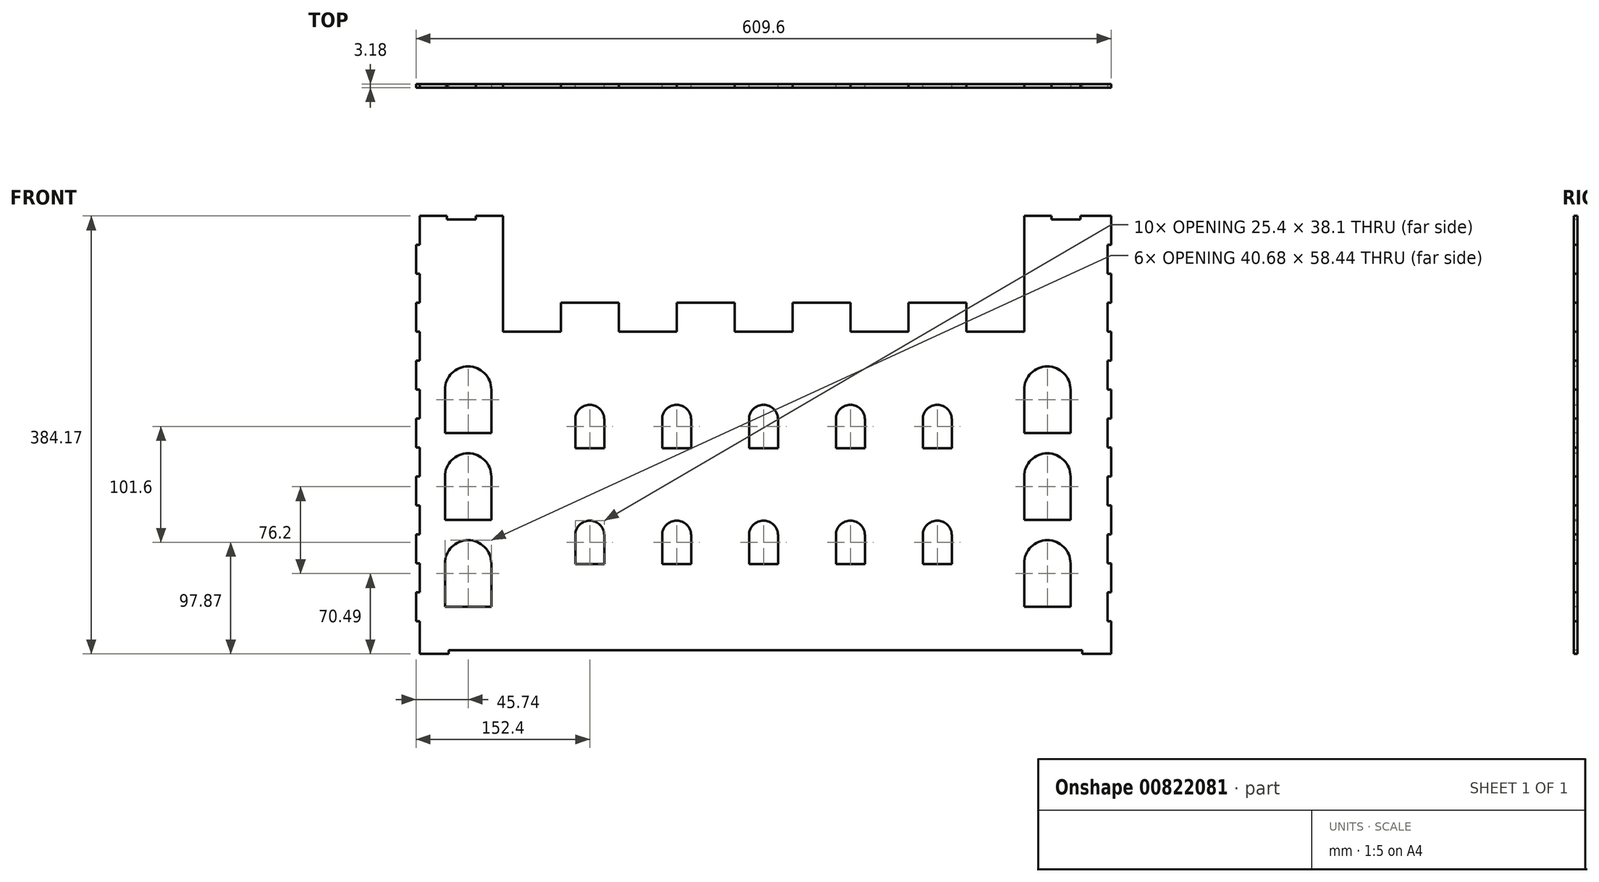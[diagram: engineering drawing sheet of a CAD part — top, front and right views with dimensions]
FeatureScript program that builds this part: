
annotation { "Feature Type Name" : "Feature", "Feature Type Description" : "" }
export const myFeature = defineFeature(function(context is Context, id is Id, definition is map)
    precondition{}
    {
        {
            var Q0;
            Q0=qCreatedBy(makeId("Front.planeOp"),FACE);
            var sketch = newSketch(context, id + "F0", { "sketchPlane" : qUnion([Q0])});
            skLineSegment(sketch, "E0.bottom", {"start": v(-304.8, 152.4) * mm, "end": v(-228.6, 152.4) * mm});
            skLineSegment(sketch, "E0.top", {"start": v(-304.8, -152.4) * mm, "end": v(304.8, -152.4) * mm});
            skLineSegment(sketch, "E0.left", {"start": v(-304.8, 152.4) * mm, "end": v(-304.8, -152.4) * mm});
            skLineSegment(sketch, "E0.right", {"start": v(304.8, 152.4) * mm, "end": v(304.8, -152.4) * mm});
            skPoint(sketch, "E0.middle", {"position": v(0, 0) * mm});
            skLineSegment(sketch, "E1", {"start": v(-304.8, 152.4) * mm, "end": v(-304.8, 228.6) * mm});
            skLineSegment(sketch, "E2", {"start": v(-304.8, 228.6) * mm, "end": v(-228.6, 228.6) * mm});
            skLineSegment(sketch, "E3", {"start": v(-228.6, 228.6) * mm, "end": v(-228.6, 152.4) * mm});
            skLineSegment(sketch, "E4", {"start": v(304.8, 152.4) * mm, "end": v(304.8, 228.6) * mm});
            skLineSegment(sketch, "E5", {"start": v(304.8, 228.6) * mm, "end": v(228.6, 228.6) * mm});
            skLineSegment(sketch, "E6", {"start": v(228.6, 228.6) * mm, "end": v(228.6, 152.4) * mm});
            skLineSegment(sketch, "E7", {"start": v(-228.6, 152.4) * mm, "end": v(-228.6, 127) * mm});
            skLineSegment(sketch, "E8", {"start": v(-228.6, 127) * mm, "end": v(-177.8, 127) * mm});
            skLineSegment(sketch, "E9", {"start": v(-177.8, 127) * mm, "end": v(-177.8, 152.4) * mm});
            skLineSegment(sketch, "E10.1.0.0", {"start": v(-76.2, 127) * mm, "end": v(-76.2, 152.4) * mm});
            skLineSegment(sketch, "E10.1.0.1", {"start": v(-127, 152.4) * mm, "end": v(-127, 127) * mm});
            skLineSegment(sketch, "E10.1.0.2", {"start": v(-127, 127) * mm, "end": v(-76.2, 127) * mm});
            skLineSegment(sketch, "E10.2.0.0", {"start": v(25.4, 127) * mm, "end": v(25.4, 152.4) * mm});
            skLineSegment(sketch, "E10.2.0.1", {"start": v(-25.4, 152.4) * mm, "end": v(-25.4, 127) * mm});
            skLineSegment(sketch, "E10.2.0.2", {"start": v(-25.4, 127) * mm, "end": v(25.4, 127) * mm});
            skLineSegment(sketch, "E10.3.0.0", {"start": v(127, 127) * mm, "end": v(127, 152.4) * mm});
            skLineSegment(sketch, "E10.3.0.1", {"start": v(76.2, 152.4) * mm, "end": v(76.2, 127) * mm});
            skLineSegment(sketch, "E10.3.0.2", {"start": v(76.2, 127) * mm, "end": v(127, 127) * mm});
            skLineSegment(sketch, "E10.4.0.0", {"start": v(228.6, 127) * mm, "end": v(228.6, 152.4) * mm});
            skLineSegment(sketch, "E10.4.0.1", {"start": v(177.8, 152.4) * mm, "end": v(177.8, 127) * mm});
            skLineSegment(sketch, "E10.4.0.2", {"start": v(177.8, 127) * mm, "end": v(228.6, 127) * mm});
            skLineSegment(sketch, "E10.direction1", {"start": v(-177.8, 127) * mm, "end": v(-76.2, 127) * mm, "construction": true});
            skLineSegment(sketch, "E11.trimOffspring", {"start": v(-177.8, 152.4) * mm, "end": v(-127, 152.4) * mm});
            skLineSegment(sketch, "E12.trimOffspring", {"start": v(-76.2, 152.4) * mm, "end": v(-25.4, 152.4) * mm});
            skLineSegment(sketch, "E13.trimOffspring", {"start": v(25.4, 152.4) * mm, "end": v(76.2, 152.4) * mm});
            skLineSegment(sketch, "E14.trimOffspring", {"start": v(127, 152.4) * mm, "end": v(177.8, 152.4) * mm});
            skLineSegment(sketch, "E15.trimOffspring", {"start": v(228.6, 152.4) * mm, "end": v(304.8, 152.4) * mm});
            skSolve(sketch);
        }
        {
            var Q0;
            Q0 = qSketchRegion(id + "F0", true);
            extrude(context, id + "F1", {"entities" : qUnion([Q0]), "depth" : 3.17 * mm, "offsetDistance" : 25.4 * mm});
        }
        {
            var Q0;
            Q0=makeQuery(id+"F1.opExtrude","CAP_FACE",FACE,{"disambiguationData":[OSD([sQuery(id+"F0.wireOp",EDGE,"E0.top"),sQuery(id+"F0.wireOp",EDGE,"E0.left"),sQuery(id+"F0.wireOp",EDGE,"E0.right"),sQuery(id+"F0.wireOp",EDGE,"E1"),sQuery(id+"F0.wireOp",EDGE,"E2"),sQuery(id+"F0.wireOp",EDGE,"E3"),sQuery(id+"F0.wireOp",EDGE,"E4"),sQuery(id+"F0.wireOp",EDGE,"E5"),sQuery(id+"F0.wireOp",EDGE,"E6"),sQuery(id+"F0.wireOp",EDGE,"E7"),sQuery(id+"F0.wireOp",EDGE,"E8"),sQuery(id+"F0.wireOp",EDGE,"E9"),sQuery(id+"F0.wireOp",EDGE,"E10.1.0.0"),sQuery(id+"F0.wireOp",EDGE,"E10.1.0.1"),sQuery(id+"F0.wireOp",EDGE,"E10.1.0.2"),sQuery(id+"F0.wireOp",EDGE,"E10.2.0.0"),sQuery(id+"F0.wireOp",EDGE,"E10.2.0.1"),sQuery(id+"F0.wireOp",EDGE,"E10.2.0.2"),sQuery(id+"F0.wireOp",EDGE,"E10.3.0.0"),sQuery(id+"F0.wireOp",EDGE,"E10.3.0.1"),sQuery(id+"F0.wireOp",EDGE,"E10.3.0.2"),sQuery(id+"F0.wireOp",EDGE,"E10.4.0.0"),sQuery(id+"F0.wireOp",EDGE,"E10.4.0.1"),sQuery(id+"F0.wireOp",EDGE,"E10.4.0.2"),sQuery(id+"F0.wireOp",EDGE,"E11.trimOffspring"),sQuery(id+"F0.wireOp",EDGE,"E12.trimOffspring"),sQuery(id+"F0.wireOp",EDGE,"E13.trimOffspring"),sQuery(id+"F0.wireOp",EDGE,"E14.trimOffspring")])],"isStart":false});
            var sketch = newSketch(context, id + "F2", { "sketchPlane" : qUnion([Q0])});
            skLineSegment(sketch, "E16.bottom", {"start": v(-304.8, 127) * mm, "end": v(-301.63, 127) * mm});
            skLineSegment(sketch, "E16.top", {"start": v(-304.8, 101.6) * mm, "end": v(-301.63, 101.6) * mm});
            skLineSegment(sketch, "E16.left", {"start": v(-304.8, 127) * mm, "end": v(-304.8, 101.6) * mm});
            skLineSegment(sketch, "E16.right", {"start": v(-301.63, 127) * mm, "end": v(-301.63, 101.6) * mm});
            skLineSegment(sketch, "E17.0.1.0", {"start": v(-304.8, 76.2) * mm, "end": v(-301.63, 76.2) * mm});
            skLineSegment(sketch, "E17.0.1.1", {"start": v(-301.63, 76.2) * mm, "end": v(-301.63, 50.8) * mm});
            skLineSegment(sketch, "E17.0.1.2", {"start": v(-304.8, 50.8) * mm, "end": v(-301.63, 50.8) * mm});
            skLineSegment(sketch, "E17.0.2.0", {"start": v(-304.8, 25.4) * mm, "end": v(-301.63, 25.4) * mm});
            skLineSegment(sketch, "E17.0.2.1", {"start": v(-301.63, 25.4) * mm, "end": v(-301.63, 0) * mm});
            skLineSegment(sketch, "E17.0.2.2", {"start": v(-304.8, 0) * mm, "end": v(-301.63, 0) * mm});
            skLineSegment(sketch, "E17.0.3.0", {"start": v(-304.8, -25.4) * mm, "end": v(-301.63, -25.4) * mm});
            skLineSegment(sketch, "E17.0.3.1", {"start": v(-301.63, -25.4) * mm, "end": v(-301.63, -50.8) * mm});
            skLineSegment(sketch, "E17.0.3.2", {"start": v(-304.8, -50.8) * mm, "end": v(-301.63, -50.8) * mm});
            skLineSegment(sketch, "E17.0.4.0", {"start": v(-304.8, -76.2) * mm, "end": v(-301.63, -76.2) * mm});
            skLineSegment(sketch, "E17.0.4.1", {"start": v(-301.63, -76.2) * mm, "end": v(-301.63, -101.6) * mm});
            skLineSegment(sketch, "E17.0.4.2", {"start": v(-304.8, -101.6) * mm, "end": v(-301.63, -101.6) * mm});
            skLineSegment(sketch, "E17.0.5.0", {"start": v(-304.8, -127) * mm, "end": v(-301.63, -127) * mm});
            skLineSegment(sketch, "E17.0.5.1", {"start": v(-301.63, -127) * mm, "end": v(-301.63, -152.4) * mm});
            skLineSegment(sketch, "E17.0.5.2", {"start": v(-304.8, -152.4) * mm, "end": v(-301.63, -152.4) * mm});
            skLineSegment(sketch, "E17.direction1", {"start": v(-304.8, 127) * mm, "end": v(-279.4, 127) * mm, "construction": true});
            skLineSegment(sketch, "E17.direction2", {"start": v(-304.8, 127) * mm, "end": v(-304.8, 76.2) * mm, "construction": true});
            skLineSegment(sketch, "E18.0.1.0", {"start": v(-301.63, 177.8) * mm, "end": v(-301.63, 152.4) * mm});
            skLineSegment(sketch, "E18.0.1.1", {"start": v(-304.8, 152.4) * mm, "end": v(-301.63, 152.4) * mm});
            skLineSegment(sketch, "E18.0.2.0", {"start": v(-301.63, 228.6) * mm, "end": v(-301.63, 203.2) * mm});
            skLineSegment(sketch, "E18.0.2.1", {"start": v(-304.8, 203.2) * mm, "end": v(-301.63, 203.2) * mm});
            skLineSegment(sketch, "E18.direction1", {"start": v(-301.63, 101.6) * mm, "end": v(-276.23, 101.6) * mm, "construction": true});
            skLineSegment(sketch, "E18.direction2", {"start": v(-301.63, 101.6) * mm, "end": v(-301.63, 152.4) * mm, "construction": true});
            skLineSegment(sketch, "E19", {"start": v(-301.63, 177.8) * mm, "end": v(-304.8, 177.8) * mm});
            skLineSegment(sketch, "E20.bottom", {"start": v(304.8, 203.2) * mm, "end": v(301.63, 203.2) * mm});
            skLineSegment(sketch, "E20.top", {"start": v(304.8, 177.8) * mm, "end": v(301.63, 177.8) * mm});
            skLineSegment(sketch, "E20.left", {"start": v(304.8, 203.2) * mm, "end": v(304.8, 177.8) * mm});
            skLineSegment(sketch, "E20.right", {"start": v(301.63, 203.2) * mm, "end": v(301.63, 177.8) * mm});
            skLineSegment(sketch, "E21.0.1.0", {"start": v(304.8, 152.4) * mm, "end": v(301.63, 152.4) * mm});
            skLineSegment(sketch, "E21.0.1.1", {"start": v(301.63, 152.4) * mm, "end": v(301.63, 127) * mm});
            skLineSegment(sketch, "E21.0.1.2", {"start": v(304.8, 127) * mm, "end": v(301.63, 127) * mm});
            skLineSegment(sketch, "E21.0.2.0", {"start": v(304.8, 101.6) * mm, "end": v(301.63, 101.6) * mm});
            skLineSegment(sketch, "E21.0.2.1", {"start": v(301.63, 101.6) * mm, "end": v(301.63, 76.2) * mm});
            skLineSegment(sketch, "E21.0.2.2", {"start": v(304.8, 76.2) * mm, "end": v(301.63, 76.2) * mm});
            skLineSegment(sketch, "E21.0.3.0", {"start": v(304.8, 50.8) * mm, "end": v(301.63, 50.8) * mm});
            skLineSegment(sketch, "E21.0.3.1", {"start": v(301.63, 50.8) * mm, "end": v(301.63, 25.4) * mm});
            skLineSegment(sketch, "E21.0.3.2", {"start": v(304.8, 25.4) * mm, "end": v(301.63, 25.4) * mm});
            skLineSegment(sketch, "E21.0.4.0", {"start": v(304.8, 0) * mm, "end": v(301.63, 0) * mm});
            skLineSegment(sketch, "E21.0.4.1", {"start": v(301.63, 0) * mm, "end": v(301.63, -25.4) * mm});
            skLineSegment(sketch, "E21.0.4.2", {"start": v(304.8, -25.4) * mm, "end": v(301.63, -25.4) * mm});
            skLineSegment(sketch, "E21.0.5.0", {"start": v(304.8, -50.8) * mm, "end": v(301.63, -50.8) * mm});
            skLineSegment(sketch, "E21.0.5.1", {"start": v(301.63, -50.8) * mm, "end": v(301.63, -76.2) * mm});
            skLineSegment(sketch, "E21.0.5.2", {"start": v(304.8, -76.2) * mm, "end": v(301.63, -76.2) * mm});
            skLineSegment(sketch, "E21.0.6.0", {"start": v(304.8, -101.6) * mm, "end": v(301.63, -101.6) * mm});
            skLineSegment(sketch, "E21.0.6.1", {"start": v(301.63, -101.6) * mm, "end": v(301.63, -127) * mm});
            skLineSegment(sketch, "E21.0.6.2", {"start": v(304.8, -127) * mm, "end": v(301.63, -127) * mm});
            skLineSegment(sketch, "E21.direction1", {"start": v(301.63, 203.2) * mm, "end": v(327.03, 203.2) * mm, "construction": true});
            skLineSegment(sketch, "E21.direction2", {"start": v(301.63, 203.2) * mm, "end": v(301.63, 152.4) * mm, "construction": true});
            skSolve(sketch);
        }
        {
            var Q0;
            Q0 = qSketchRegion(id + "F2", true);
            var Q1;
            {var subQ0=sQuery(id+"F2.wireOp",EDGE,"E17.0.1.0");Q1=makeQuery(id+"F2.imprint","IMPRINT",FACE,{"disambiguationData":[TD([[makeQuery(id+"F2.imprint","IMPRINT",EDGE,{"derivedFrom":subQ0}),-1.0]])]});}
            var Q2;
            {var subQ0=sQuery(id+"F2.wireOp",EDGE,"E17.0.2.0");Q2=makeQuery(id+"F2.imprint","IMPRINT",FACE,{"disambiguationData":[TD([[makeQuery(id+"F2.imprint","IMPRINT",EDGE,{"derivedFrom":subQ0}),-1.0]])]});}
            var Q3;
            {var subQ0=sQuery(id+"F2.wireOp",EDGE,"E17.0.3.0");Q3=makeQuery(id+"F2.imprint","IMPRINT",FACE,{"disambiguationData":[TD([[makeQuery(id+"F2.imprint","IMPRINT",EDGE,{"derivedFrom":subQ0}),-1.0]])]});}
            var Q4;
            {var subQ0=sQuery(id+"F2.wireOp",EDGE,"E17.0.4.0");Q4=makeQuery(id+"F2.imprint","IMPRINT",FACE,{"disambiguationData":[TD([[makeQuery(id+"F2.imprint","IMPRINT",EDGE,{"derivedFrom":subQ0}),-1.0]])]});}
            var Q5;
            {var subQ0=sQuery(id+"F2.wireOp",EDGE,"E17.0.5.0");Q5=makeQuery(id+"F2.imprint","IMPRINT",FACE,{"disambiguationData":[TD([[makeQuery(id+"F2.imprint","IMPRINT",EDGE,{"derivedFrom":subQ0}),-1.0]])]});}
            extrude(context, id + "F3", {"entities" : qUnion([Q0, Q1, Q2, Q3, Q4, Q5]), "operationType" : NewBodyOperationType.REMOVE, "oppositeDirection" : true, "depth" : 25.4 * mm, "offsetDistance" : 25.4 * mm});
        }
        {
            var Q0;
            Q0 = qSketchRegion(id + "F2", true);
            var Q1;
            Q1=makeQuery(id+"F2.imprint","IMPRINT",FACE,{"disambiguationData":[TD([[makeQuery(id+"F2.imprint","IMPRINT",EDGE,{"derivedFrom":sQuery(id+"F2.wireOp",EDGE,"E18.0.1.0")}),-1.0]])]});
            var Q2;
            {var subQ0=sQuery(id+"F2.wireOp",EDGE,"E18.0.2.0");Q2=makeQuery(id+"F2.imprint","IMPRINT",FACE,{"disambiguationData":[TD([[makeQuery(id+"F2.imprint","IMPRINT",EDGE,{"derivedFrom":subQ0}),-1.0]])]});}
            extrude(context, id + "F4", {"entities" : qUnion([Q0, Q1, Q2]), "operationType" : NewBodyOperationType.REMOVE, "oppositeDirection" : true, "depth" : 25.4 * mm, "offsetDistance" : 25.4 * mm});
        }
        {
            var Q0;
            {var subQ0=sQuery(id+"F2.wireOp",EDGE,"E21.0.1.0");Q0=makeQuery(id+"F2.imprint","IMPRINT",FACE,{"disambiguationData":[TD([[makeQuery(id+"F2.imprint","IMPRINT",EDGE,{"derivedFrom":subQ0}),1.0]])]});}
            var Q1;
            {var subQ0=sQuery(id+"F2.wireOp",EDGE,"E21.0.2.0");Q1=makeQuery(id+"F2.imprint","IMPRINT",FACE,{"disambiguationData":[TD([[makeQuery(id+"F2.imprint","IMPRINT",EDGE,{"derivedFrom":subQ0}),1.0]])]});}
            var Q2;
            {var subQ0=sQuery(id+"F2.wireOp",EDGE,"E21.0.3.0");Q2=makeQuery(id+"F2.imprint","IMPRINT",FACE,{"disambiguationData":[TD([[makeQuery(id+"F2.imprint","IMPRINT",EDGE,{"derivedFrom":subQ0}),1.0]])]});}
            var Q3;
            {var subQ0=sQuery(id+"F2.wireOp",EDGE,"E21.0.4.0");Q3=makeQuery(id+"F2.imprint","IMPRINT",FACE,{"disambiguationData":[TD([[makeQuery(id+"F2.imprint","IMPRINT",EDGE,{"derivedFrom":subQ0}),1.0]])]});}
            var Q4;
            {var subQ0=sQuery(id+"F2.wireOp",EDGE,"E21.0.5.0");Q4=makeQuery(id+"F2.imprint","IMPRINT",FACE,{"disambiguationData":[TD([[makeQuery(id+"F2.imprint","IMPRINT",EDGE,{"derivedFrom":subQ0}),1.0]])]});}
            var Q5;
            {var subQ0=sQuery(id+"F2.wireOp",EDGE,"E21.0.6.0");Q5=makeQuery(id+"F2.imprint","IMPRINT",FACE,{"disambiguationData":[TD([[makeQuery(id+"F2.imprint","IMPRINT",EDGE,{"derivedFrom":subQ0}),1.0]])]});}
            extrude(context, id + "F5", {"entities" : qUnion([Q0, Q1, Q2, Q3, Q4, Q5]), "operationType" : NewBodyOperationType.REMOVE, "oppositeDirection" : true, "depth" : 25.4 * mm, "offsetDistance" : 25.4 * mm});
        }
        {
            var Q0;
            Q0=makeQuery(id+"F1.opExtrude","CAP_FACE",FACE,{"disambiguationData":[OSD([sQuery(id+"F0.wireOp",EDGE,"E0.top"),sQuery(id+"F0.wireOp",EDGE,"E0.left"),sQuery(id+"F0.wireOp",EDGE,"E0.right"),sQuery(id+"F0.wireOp",EDGE,"E1"),sQuery(id+"F0.wireOp",EDGE,"E2"),sQuery(id+"F0.wireOp",EDGE,"E3"),sQuery(id+"F0.wireOp",EDGE,"E4"),sQuery(id+"F0.wireOp",EDGE,"E5"),sQuery(id+"F0.wireOp",EDGE,"E6"),sQuery(id+"F0.wireOp",EDGE,"E7"),sQuery(id+"F0.wireOp",EDGE,"E8"),sQuery(id+"F0.wireOp",EDGE,"E9"),sQuery(id+"F0.wireOp",EDGE,"E10.1.0.0"),sQuery(id+"F0.wireOp",EDGE,"E10.1.0.1"),sQuery(id+"F0.wireOp",EDGE,"E10.1.0.2"),sQuery(id+"F0.wireOp",EDGE,"E10.2.0.0"),sQuery(id+"F0.wireOp",EDGE,"E10.2.0.1"),sQuery(id+"F0.wireOp",EDGE,"E10.2.0.2"),sQuery(id+"F0.wireOp",EDGE,"E10.3.0.0"),sQuery(id+"F0.wireOp",EDGE,"E10.3.0.1"),sQuery(id+"F0.wireOp",EDGE,"E10.3.0.2"),sQuery(id+"F0.wireOp",EDGE,"E10.4.0.0"),sQuery(id+"F0.wireOp",EDGE,"E10.4.0.1"),sQuery(id+"F0.wireOp",EDGE,"E10.4.0.2"),sQuery(id+"F0.wireOp",EDGE,"E11.trimOffspring"),sQuery(id+"F0.wireOp",EDGE,"E12.trimOffspring"),sQuery(id+"F0.wireOp",EDGE,"E13.trimOffspring"),sQuery(id+"F0.wireOp",EDGE,"E14.trimOffspring")])],"isStart":false});
            var sketch = newSketch(context, id + "F6", { "sketchPlane" : qUnion([Q0])});
            skLineSegment(sketch, "E22.bottom", {"start": v(-279.4, 76.2) * mm, "end": v(-238.72, 76.2) * mm});
            skLineSegment(sketch, "E22.top", {"start": v(-279.4, 38.1) * mm, "end": v(-238.72, 38.1) * mm});
            skLineSegment(sketch, "E22.left", {"start": v(-279.4, 76.2) * mm, "end": v(-279.4, 38.1) * mm});
            skLineSegment(sketch, "E22.right", {"start": v(-238.72, 76.2) * mm, "end": v(-238.72, 38.1) * mm});
            skArc(sketch, "E23", {"start": v(-238.72, 76.2) * mm, "mid": v(-259.06, 96.54) * mm, "end": v(-279.4, 76.2) * mm});
            skLineSegment(sketch, "E24.0.1.0", {"start": v(-279.4, 0) * mm, "end": v(-238.72, 0) * mm});
            skLineSegment(sketch, "E24.0.1.1", {"start": v(-279.4, -38.1) * mm, "end": v(-238.72, -38.1) * mm});
            skLineSegment(sketch, "E24.0.1.2", {"start": v(-279.4, 0) * mm, "end": v(-279.4, -38.1) * mm});
            skLineSegment(sketch, "E24.0.1.3", {"start": v(-238.72, 0) * mm, "end": v(-238.72, -38.1) * mm});
            skArc(sketch, "E24.0.1.4", {"start": v(-238.72, 0) * mm, "mid": v(-259.06, 20.34) * mm, "end": v(-279.4, 0) * mm});
            skLineSegment(sketch, "E24.0.2.0", {"start": v(-279.4, -76.2) * mm, "end": v(-238.72, -76.2) * mm});
            skLineSegment(sketch, "E24.0.2.1", {"start": v(-279.4, -114.3) * mm, "end": v(-238.72, -114.3) * mm});
            skLineSegment(sketch, "E24.0.2.2", {"start": v(-279.4, -76.2) * mm, "end": v(-279.4, -114.3) * mm});
            skLineSegment(sketch, "E24.0.2.3", {"start": v(-238.72, -76.2) * mm, "end": v(-238.72, -114.3) * mm});
            skArc(sketch, "E24.0.2.4", {"start": v(-238.72, -76.2) * mm, "mid": v(-259.06, -55.86) * mm, "end": v(-279.4, -76.2) * mm});
            skLineSegment(sketch, "E24.1.0.0", {"start": v(228.6, 76.2) * mm, "end": v(269.28, 76.2) * mm});
            skLineSegment(sketch, "E24.1.0.1", {"start": v(228.6, 38.1) * mm, "end": v(269.28, 38.1) * mm});
            skLineSegment(sketch, "E24.1.0.2", {"start": v(228.6, 76.2) * mm, "end": v(228.6, 38.1) * mm});
            skLineSegment(sketch, "E24.1.0.3", {"start": v(269.28, 76.2) * mm, "end": v(269.28, 38.1) * mm});
            skArc(sketch, "E24.1.0.4", {"start": v(269.28, 76.2) * mm, "mid": v(248.94, 96.54) * mm, "end": v(228.6, 76.2) * mm});
            skLineSegment(sketch, "E24.1.1.0", {"start": v(228.6, 0) * mm, "end": v(269.28, 0) * mm});
            skLineSegment(sketch, "E24.1.1.1", {"start": v(228.6, -38.1) * mm, "end": v(269.28, -38.1) * mm});
            skLineSegment(sketch, "E24.1.1.2", {"start": v(228.6, 0) * mm, "end": v(228.6, -38.1) * mm});
            skLineSegment(sketch, "E24.1.1.3", {"start": v(269.28, 0) * mm, "end": v(269.28, -38.1) * mm});
            skArc(sketch, "E24.1.1.4", {"start": v(269.28, 0) * mm, "mid": v(248.94, 20.34) * mm, "end": v(228.6, 0) * mm});
            skLineSegment(sketch, "E24.1.2.0", {"start": v(228.6, -76.2) * mm, "end": v(269.28, -76.2) * mm});
            skLineSegment(sketch, "E24.1.2.1", {"start": v(228.6, -114.3) * mm, "end": v(269.28, -114.3) * mm});
            skLineSegment(sketch, "E24.1.2.2", {"start": v(228.6, -76.2) * mm, "end": v(228.6, -114.3) * mm});
            skLineSegment(sketch, "E24.1.2.3", {"start": v(269.28, -76.2) * mm, "end": v(269.28, -114.3) * mm});
            skArc(sketch, "E24.1.2.4", {"start": v(269.28, -76.2) * mm, "mid": v(248.94, -55.86) * mm, "end": v(228.6, -76.2) * mm});
            skLineSegment(sketch, "E24.direction1", {"start": v(-279.4, 38.1) * mm, "end": v(228.6, 38.1) * mm, "construction": true});
            skLineSegment(sketch, "E24.direction2", {"start": v(-279.4, 38.1) * mm, "end": v(-279.4, -38.1) * mm, "construction": true});
            skSolve(sketch);
        }
        {
            var Q0;
            Q0 = qSketchRegion(id + "F6", true);
            extrude(context, id + "F7", {"entities" : qUnion([Q0]), "operationType" : NewBodyOperationType.REMOVE, "oppositeDirection" : true, "depth" : 25.4 * mm, "offsetDistance" : 25.4 * mm});
        }
        {
            var Q0;
            Q0=makeQuery(id+"F1.opExtrude","CAP_FACE",FACE,{"disambiguationData":[OSD([sQuery(id+"F0.wireOp",EDGE,"E0.top"),sQuery(id+"F0.wireOp",EDGE,"E0.left"),sQuery(id+"F0.wireOp",EDGE,"E0.right"),sQuery(id+"F0.wireOp",EDGE,"E1"),sQuery(id+"F0.wireOp",EDGE,"E2"),sQuery(id+"F0.wireOp",EDGE,"E3"),sQuery(id+"F0.wireOp",EDGE,"E4"),sQuery(id+"F0.wireOp",EDGE,"E5"),sQuery(id+"F0.wireOp",EDGE,"E6"),sQuery(id+"F0.wireOp",EDGE,"E7"),sQuery(id+"F0.wireOp",EDGE,"E8"),sQuery(id+"F0.wireOp",EDGE,"E9"),sQuery(id+"F0.wireOp",EDGE,"E10.1.0.0"),sQuery(id+"F0.wireOp",EDGE,"E10.1.0.1"),sQuery(id+"F0.wireOp",EDGE,"E10.1.0.2"),sQuery(id+"F0.wireOp",EDGE,"E10.2.0.0"),sQuery(id+"F0.wireOp",EDGE,"E10.2.0.1"),sQuery(id+"F0.wireOp",EDGE,"E10.2.0.2"),sQuery(id+"F0.wireOp",EDGE,"E10.3.0.0"),sQuery(id+"F0.wireOp",EDGE,"E10.3.0.1"),sQuery(id+"F0.wireOp",EDGE,"E10.3.0.2"),sQuery(id+"F0.wireOp",EDGE,"E10.4.0.0"),sQuery(id+"F0.wireOp",EDGE,"E10.4.0.1"),sQuery(id+"F0.wireOp",EDGE,"E10.4.0.2"),sQuery(id+"F0.wireOp",EDGE,"E11.trimOffspring"),sQuery(id+"F0.wireOp",EDGE,"E12.trimOffspring"),sQuery(id+"F0.wireOp",EDGE,"E13.trimOffspring"),sQuery(id+"F0.wireOp",EDGE,"E14.trimOffspring")])],"isStart":true});
            var sketch = newSketch(context, id + "F8", { "sketchPlane" : qUnion([Q0])});
            skLineSegment(sketch, "E25.bottom", {"start": v(-165.1, 50.25) * mm, "end": v(-139.7, 50.25) * mm});
            skLineSegment(sketch, "E25.top", {"start": v(-165.1, 24.85) * mm, "end": v(-139.7, 24.85) * mm});
            skLineSegment(sketch, "E25.left", {"start": v(-165.1, 50.25) * mm, "end": v(-165.1, 24.85) * mm});
            skLineSegment(sketch, "E25.right", {"start": v(-139.7, 50.25) * mm, "end": v(-139.7, 24.85) * mm});
            skArc(sketch, "E26", {"start": v(-139.7, 50.25) * mm, "mid": v(-152.4, 62.95) * mm, "end": v(-165.1, 50.25) * mm});
            skArc(sketch, "E27.0.1.0", {"start": v(-139.7, -51.35) * mm, "mid": v(-152.4, -38.65) * mm, "end": v(-165.1, -51.35) * mm});
            skLineSegment(sketch, "E27.0.1.1", {"start": v(-139.7, -51.35) * mm, "end": v(-139.7, -76.75) * mm});
            skLineSegment(sketch, "E27.0.1.2", {"start": v(-165.1, -51.35) * mm, "end": v(-165.1, -76.75) * mm});
            skLineSegment(sketch, "E27.0.1.3", {"start": v(-165.1, -76.75) * mm, "end": v(-139.7, -76.75) * mm});
            skLineSegment(sketch, "E27.0.1.4", {"start": v(-165.1, -51.35) * mm, "end": v(-139.7, -51.35) * mm});
            skArc(sketch, "E27.1.0.0", {"start": v(-63.5, 50.25) * mm, "mid": v(-76.2, 62.95) * mm, "end": v(-88.9, 50.25) * mm});
            skLineSegment(sketch, "E27.1.0.1", {"start": v(-63.5, 50.25) * mm, "end": v(-63.5, 24.85) * mm});
            skLineSegment(sketch, "E27.1.0.2", {"start": v(-88.9, 50.25) * mm, "end": v(-88.9, 24.85) * mm});
            skLineSegment(sketch, "E27.1.0.3", {"start": v(-88.9, 24.85) * mm, "end": v(-63.5, 24.85) * mm});
            skLineSegment(sketch, "E27.1.0.4", {"start": v(-88.9, 50.25) * mm, "end": v(-63.5, 50.25) * mm});
            skArc(sketch, "E27.1.1.0", {"start": v(-63.5, -51.35) * mm, "mid": v(-76.2, -38.65) * mm, "end": v(-88.9, -51.35) * mm});
            skLineSegment(sketch, "E27.1.1.1", {"start": v(-63.5, -51.35) * mm, "end": v(-63.5, -76.75) * mm});
            skLineSegment(sketch, "E27.1.1.2", {"start": v(-88.9, -51.35) * mm, "end": v(-88.9, -76.75) * mm});
            skLineSegment(sketch, "E27.1.1.3", {"start": v(-88.9, -76.75) * mm, "end": v(-63.5, -76.75) * mm});
            skLineSegment(sketch, "E27.1.1.4", {"start": v(-88.9, -51.35) * mm, "end": v(-63.5, -51.35) * mm});
            skArc(sketch, "E27.2.0.0", {"start": v(12.7, 50.25) * mm, "mid": v(0, 62.95) * mm, "end": v(-12.7, 50.25) * mm});
            skLineSegment(sketch, "E27.2.0.1", {"start": v(12.7, 50.25) * mm, "end": v(12.7, 24.85) * mm});
            skLineSegment(sketch, "E27.2.0.2", {"start": v(-12.7, 50.25) * mm, "end": v(-12.7, 24.85) * mm});
            skLineSegment(sketch, "E27.2.0.3", {"start": v(-12.7, 24.85) * mm, "end": v(12.7, 24.85) * mm});
            skLineSegment(sketch, "E27.2.0.4", {"start": v(-12.7, 50.25) * mm, "end": v(12.7, 50.25) * mm});
            skArc(sketch, "E27.2.1.0", {"start": v(12.7, -51.35) * mm, "mid": v(0, -38.65) * mm, "end": v(-12.7, -51.35) * mm});
            skLineSegment(sketch, "E27.2.1.1", {"start": v(12.7, -51.35) * mm, "end": v(12.7, -76.75) * mm});
            skLineSegment(sketch, "E27.2.1.2", {"start": v(-12.7, -51.35) * mm, "end": v(-12.7, -76.75) * mm});
            skLineSegment(sketch, "E27.2.1.3", {"start": v(-12.7, -76.75) * mm, "end": v(12.7, -76.75) * mm});
            skLineSegment(sketch, "E27.2.1.4", {"start": v(-12.7, -51.35) * mm, "end": v(12.7, -51.35) * mm});
            skArc(sketch, "E27.3.0.0", {"start": v(88.9, 50.25) * mm, "mid": v(76.2, 62.95) * mm, "end": v(63.5, 50.25) * mm});
            skLineSegment(sketch, "E27.3.0.1", {"start": v(88.9, 50.25) * mm, "end": v(88.9, 24.85) * mm});
            skLineSegment(sketch, "E27.3.0.2", {"start": v(63.5, 50.25) * mm, "end": v(63.5, 24.85) * mm});
            skLineSegment(sketch, "E27.3.0.3", {"start": v(63.5, 24.85) * mm, "end": v(88.9, 24.85) * mm});
            skLineSegment(sketch, "E27.3.0.4", {"start": v(63.5, 50.25) * mm, "end": v(88.9, 50.25) * mm});
            skArc(sketch, "E27.3.1.0", {"start": v(88.9, -51.35) * mm, "mid": v(76.2, -38.65) * mm, "end": v(63.5, -51.35) * mm});
            skLineSegment(sketch, "E27.3.1.1", {"start": v(88.9, -51.35) * mm, "end": v(88.9, -76.75) * mm});
            skLineSegment(sketch, "E27.3.1.2", {"start": v(63.5, -51.35) * mm, "end": v(63.5, -76.75) * mm});
            skLineSegment(sketch, "E27.3.1.3", {"start": v(63.5, -76.75) * mm, "end": v(88.9, -76.75) * mm});
            skLineSegment(sketch, "E27.3.1.4", {"start": v(63.5, -51.35) * mm, "end": v(88.9, -51.35) * mm});
            skArc(sketch, "E27.4.0.0", {"start": v(165.1, 50.25) * mm, "mid": v(152.4, 62.95) * mm, "end": v(139.7, 50.25) * mm});
            skLineSegment(sketch, "E27.4.0.1", {"start": v(165.1, 50.25) * mm, "end": v(165.1, 24.85) * mm});
            skLineSegment(sketch, "E27.4.0.2", {"start": v(139.7, 50.25) * mm, "end": v(139.7, 24.85) * mm});
            skLineSegment(sketch, "E27.4.0.3", {"start": v(139.7, 24.85) * mm, "end": v(165.1, 24.85) * mm});
            skLineSegment(sketch, "E27.4.0.4", {"start": v(139.7, 50.25) * mm, "end": v(165.1, 50.25) * mm});
            skArc(sketch, "E27.4.1.0", {"start": v(165.1, -51.35) * mm, "mid": v(152.4, -38.65) * mm, "end": v(139.7, -51.35) * mm});
            skLineSegment(sketch, "E27.4.1.1", {"start": v(165.1, -51.35) * mm, "end": v(165.1, -76.75) * mm});
            skLineSegment(sketch, "E27.4.1.2", {"start": v(139.7, -51.35) * mm, "end": v(139.7, -76.75) * mm});
            skLineSegment(sketch, "E27.4.1.3", {"start": v(139.7, -76.75) * mm, "end": v(165.1, -76.75) * mm});
            skLineSegment(sketch, "E27.4.1.4", {"start": v(139.7, -51.35) * mm, "end": v(165.1, -51.35) * mm});
            skLineSegment(sketch, "E27.direction1", {"start": v(-165.1, 24.85) * mm, "end": v(-88.9, 24.85) * mm, "construction": true});
            skLineSegment(sketch, "E27.direction2", {"start": v(-165.1, 24.85) * mm, "end": v(-165.1, -76.75) * mm, "construction": true});
            skSolve(sketch);
        }
        {
            var Q0;
            Q0 = qSketchRegion(id + "F8", true);
            extrude(context, id + "F9", {"entities" : qUnion([Q0]), "operationType" : NewBodyOperationType.REMOVE, "oppositeDirection" : true, "depth" : 25.4 * mm, "offsetDistance" : 25.4 * mm});
        }
        {
            var Q0;
            Q0=makeQuery(id+"F1.opExtrude","SWEPT_FACE",FACE,{"disambiguationData":[OSD([sQuery(id+"F0.wireOp",EDGE,"E0.top")])]});
            var sketch = newSketch(context, id + "F10", { "sketchPlane" : qUnion([Q0])});
            skLineSegment(sketch, "E28.bottom", {"start": v(304.8, 0) * mm, "end": v(279.4, 0) * mm});
            skLineSegment(sketch, "E28.top", {"start": v(304.8, 3.17) * mm, "end": v(279.4, 3.17) * mm});
            skLineSegment(sketch, "E28.left", {"start": v(304.8, 0) * mm, "end": v(304.8, 3.17) * mm});
            skLineSegment(sketch, "E28.right", {"start": v(279.4, 0) * mm, "end": v(279.4, 3.17) * mm});
            skLineSegment(sketch, "E29.bottom", {"start": v(-301.63, 0) * mm, "end": v(-276.23, 0) * mm});
            skLineSegment(sketch, "E29.top", {"start": v(-301.63, 3.17) * mm, "end": v(-276.23, 3.17) * mm});
            skLineSegment(sketch, "E29.left", {"start": v(-301.63, 0) * mm, "end": v(-301.63, 3.17) * mm});
            skLineSegment(sketch, "E29.right", {"start": v(-276.23, 0) * mm, "end": v(-276.23, 3.17) * mm});
            skSolve(sketch);
        }
        {
            var Q0;
            Q0 = qSketchRegion(id + "F10", true);
            extrude(context, id + "F11", {"entities" : qUnion([Q0]), "operationType" : NewBodyOperationType.ADD, "depth" : 3.17 * mm, "offsetDistance" : 25.4 * mm});
        }
        {
            var Q0;
            Q0=makeQuery(id+"F11.boolean.opBoolean","MERGE",FACE,{"derivedFrom":[makeQuery(id+"F1.opExtrude","CAP_FACE",FACE,{"disambiguationData":[OSD([sQuery(id+"F0.wireOp",EDGE,"E0.top"),sQuery(id+"F0.wireOp",EDGE,"E0.left"),sQuery(id+"F0.wireOp",EDGE,"E0.right"),sQuery(id+"F0.wireOp",EDGE,"E1"),sQuery(id+"F0.wireOp",EDGE,"E2"),sQuery(id+"F0.wireOp",EDGE,"E3"),sQuery(id+"F0.wireOp",EDGE,"E4"),sQuery(id+"F0.wireOp",EDGE,"E5"),sQuery(id+"F0.wireOp",EDGE,"E6"),sQuery(id+"F0.wireOp",EDGE,"E7"),sQuery(id+"F0.wireOp",EDGE,"E8"),sQuery(id+"F0.wireOp",EDGE,"E9"),sQuery(id+"F0.wireOp",EDGE,"E10.1.0.0"),sQuery(id+"F0.wireOp",EDGE,"E10.1.0.1"),sQuery(id+"F0.wireOp",EDGE,"E10.1.0.2"),sQuery(id+"F0.wireOp",EDGE,"E10.2.0.0"),sQuery(id+"F0.wireOp",EDGE,"E10.2.0.1"),sQuery(id+"F0.wireOp",EDGE,"E10.2.0.2"),sQuery(id+"F0.wireOp",EDGE,"E10.3.0.0"),sQuery(id+"F0.wireOp",EDGE,"E10.3.0.1"),sQuery(id+"F0.wireOp",EDGE,"E10.3.0.2"),sQuery(id+"F0.wireOp",EDGE,"E10.4.0.0"),sQuery(id+"F0.wireOp",EDGE,"E10.4.0.1"),sQuery(id+"F0.wireOp",EDGE,"E10.4.0.2"),sQuery(id+"F0.wireOp",EDGE,"E11.trimOffspring"),sQuery(id+"F0.wireOp",EDGE,"E12.trimOffspring"),sQuery(id+"F0.wireOp",EDGE,"E13.trimOffspring"),sQuery(id+"F0.wireOp",EDGE,"E14.trimOffspring")])],"isStart":false}),makeQuery(id+"F11.opExtrude","SWEPT_FACE",FACE,{"disambiguationData":[OSD([sQuery(id+"F10.wireOp",EDGE,"E28.top")])]}),makeQuery(id+"F11.opExtrude","SWEPT_FACE",FACE,{"disambiguationData":[OSD([sQuery(id+"F10.wireOp",EDGE,"E29.top")])]})]});
            var sketch = newSketch(context, id + "F12", { "sketchPlane" : qUnion([Q0])});
            skLineSegment(sketch, "E30.bottom", {"start": v(-277.81, 228.6) * mm, "end": v(-252.41, 228.6) * mm});
            skLineSegment(sketch, "E30.top", {"start": v(-277.81, 225.43) * mm, "end": v(-252.41, 225.43) * mm});
            skLineSegment(sketch, "E30.left", {"start": v(-277.81, 228.6) * mm, "end": v(-277.81, 225.43) * mm});
            skLineSegment(sketch, "E30.right", {"start": v(-252.41, 228.6) * mm, "end": v(-252.41, 225.43) * mm});
            skLineSegment(sketch, "E31.MirrorCS", {"start": v(252.41, 228.6) * mm, "end": v(252.41, 225.43) * mm});
            skLineSegment(sketch, "E32.MirrorCS", {"start": v(277.81, 228.6) * mm, "end": v(277.81, 225.43) * mm});
            skLineSegment(sketch, "E33.MirrorCS", {"start": v(277.81, 225.43) * mm, "end": v(252.41, 225.43) * mm});
            skLineSegment(sketch, "E34.MirrorCS", {"start": v(277.81, 228.6) * mm, "end": v(252.41, 228.6) * mm});
            skSolve(sketch);
        }
        {
            var Q0;
            Q0 = qSketchRegion(id + "F12", true);
            extrude(context, id + "F13", {"entities" : qUnion([Q0]), "operationType" : NewBodyOperationType.REMOVE, "oppositeDirection" : true, "depth" : 25.4 * mm, "offsetDistance" : 25.4 * mm});
        }
    });
